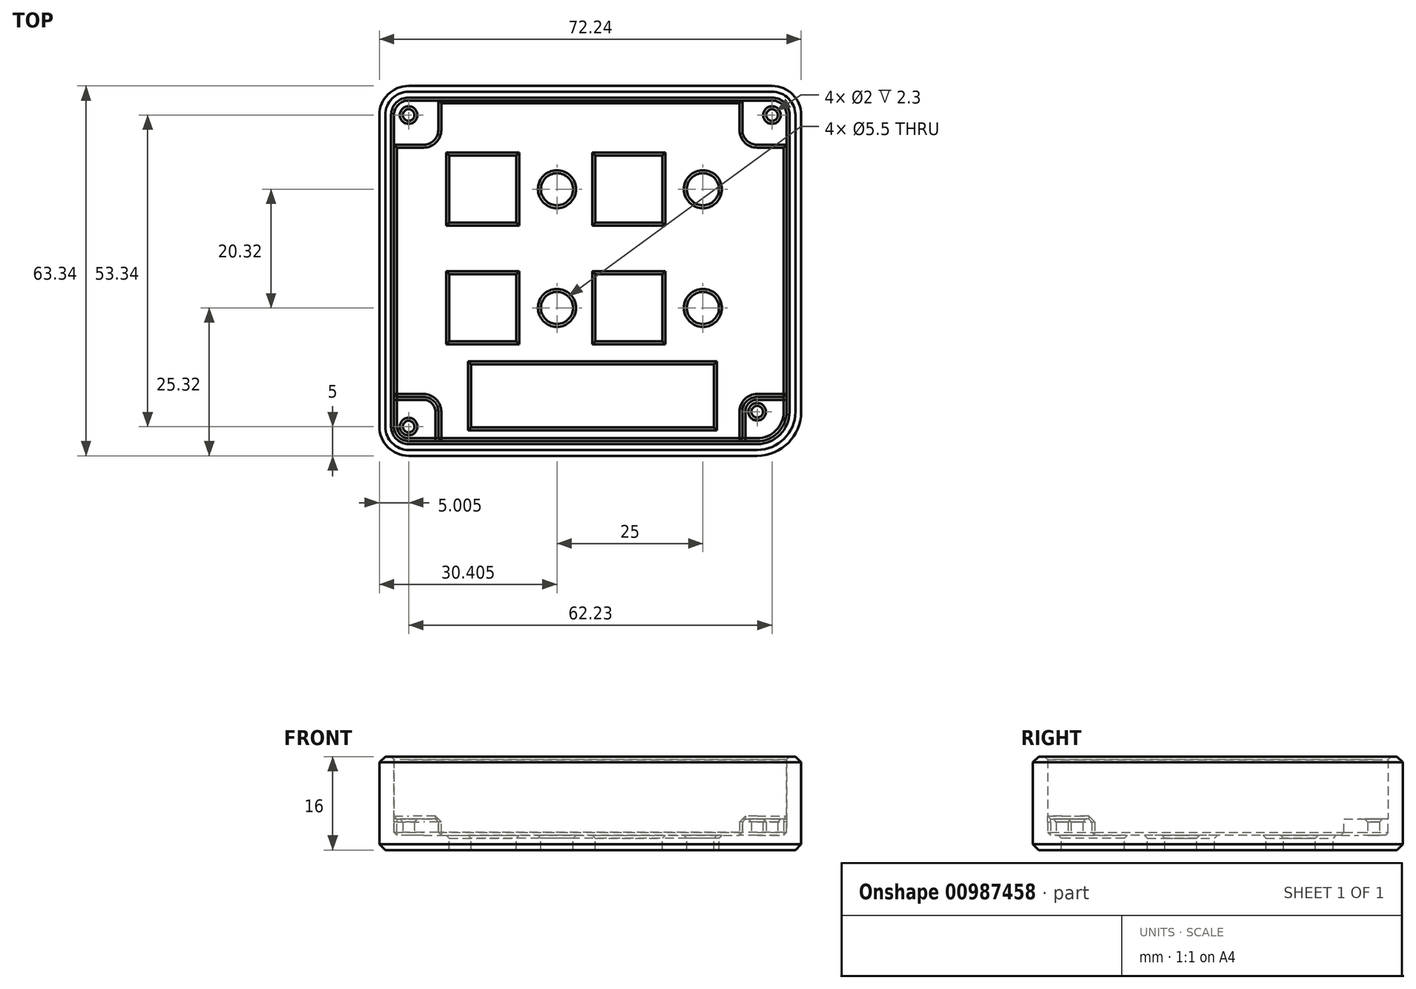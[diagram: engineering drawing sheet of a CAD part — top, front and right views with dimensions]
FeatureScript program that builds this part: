
annotation { "Feature Type Name" : "Feature", "Feature Type Description" : "" }
export const myFeature = defineFeature(function(context is Context, id is Id, definition is map)
    precondition{}
    {
        {
            var Q0;
            Q0=qCreatedBy(makeId("Top.planeOp"),FACE);
            var sketch = newSketch(context, id + "F0", { "sketchPlane" : qUnion([Q0])});
            skLineSegment(sketch, "E0.bottom", {"start": v(28.58, -31.67) * mm, "end": v(-31.11, -31.67) * mm});
            skLineSegment(sketch, "E0.top", {"start": v(31.11, 31.67) * mm, "end": v(-31.12, 31.67) * mm});
            skLineSegment(sketch, "E0.left", {"start": v(36.12, -24.13) * mm, "end": v(36.12, 26.67) * mm});
            skLineSegment(sketch, "E0.right", {"start": v(-36.11, -26.67) * mm, "end": v(-36.12, 26.67) * mm});
            skPoint(sketch, "E0.middle", {"position": v(0, 0) * mm});
            skCircle(sketch, "E1", {"center": v(-31.11, 26.67) * mm, "radius": 1 * mm});
            skCircle(sketch, "E2", {"center": v(-31.11, -26.67) * mm, "radius": 1 * mm});
            skCircle(sketch, "E3", {"center": v(31.11, 26.67) * mm, "radius": 1 * mm});
            skCircle(sketch, "E4", {"center": v(28.58, -24.13) * mm, "radius": 1 * mm});
            skPoint(sketch, "E5.visualSharp", {"position": v(-36.12, 31.67) * mm});
            skArc(sketch, "E5.filletArc", {"start": v(-31.12, 31.67) * mm, "mid": v(-34.65, 30.2) * mm, "end": v(-36.12, 26.67) * mm});
            skPoint(sketch, "E6.visualSharp", {"position": v(36.11, 31.67) * mm});
            skArc(sketch, "E6.filletArc", {"start": v(36.12, 26.67) * mm, "mid": v(34.65, 30.2) * mm, "end": v(31.11, 31.67) * mm});
            skPoint(sketch, "E7.visualSharp", {"position": v(36.12, -31.67) * mm});
            skArc(sketch, "E7.filletArc", {"start": v(28.58, -31.67) * mm, "mid": v(33.9, -29.46) * mm, "end": v(36.12, -24.13) * mm});
            skPoint(sketch, "E8.visualSharp", {"position": v(-36.11, -31.67) * mm});
            skArc(sketch, "E8.filletArc", {"start": v(-36.11, -26.67) * mm, "mid": v(-34.65, -30.2) * mm, "end": v(-31.11, -31.67) * mm});
            skLineSegment(sketch, "E9", {"start": v(-26.04, 31.67) * mm, "end": v(-26.04, 24.13) * mm});
            skLineSegment(sketch, "E10", {"start": v(-28.58, 21.59) * mm, "end": v(-36.11, 21.59) * mm});
            skPoint(sketch, "E11.visualSharp", {"position": v(-26.04, 21.59) * mm});
            skArc(sketch, "E11.filletArc", {"start": v(-28.58, 21.59) * mm, "mid": v(-26.78, 22.33) * mm, "end": v(-26.04, 24.13) * mm});
            skLineSegment(sketch, "E12.MirrorCS", {"start": v(28.58, 21.59) * mm, "end": v(36.11, 21.59) * mm});
            skArc(sketch, "E13.MirrorCS", {"start": v(28.58, 21.59) * mm, "mid": v(26.78, 22.33) * mm, "end": v(26.04, 24.13) * mm});
            skLineSegment(sketch, "E14.MirrorCS", {"start": v(26.04, 31.67) * mm, "end": v(26.04, 24.13) * mm});
            skLineSegment(sketch, "E15.MirrorCS", {"start": v(-26.04, -31.67) * mm, "end": v(-26.04, -24.13) * mm});
            skArc(sketch, "E16.MirrorCS", {"start": v(-28.58, -21.59) * mm, "mid": v(-26.78, -22.33) * mm, "end": v(-26.04, -24.13) * mm});
            skLineSegment(sketch, "E17.MirrorCS", {"start": v(-28.58, -21.59) * mm, "end": v(-36.11, -21.59) * mm});
            skLineSegment(sketch, "E18.MirrorCS", {"start": v(28.58, -21.59) * mm, "end": v(36.11, -21.59) * mm});
            skArc(sketch, "E19.MirrorCS", {"start": v(28.58, -21.59) * mm, "mid": v(26.78, -22.33) * mm, "end": v(26.04, -24.13) * mm});
            skLineSegment(sketch, "E20.MirrorCS", {"start": v(26.04, -31.67) * mm, "end": v(26.04, -24.13) * mm});
            skSolve(sketch);
        }
        {
            var Q0;
            Q0=makeQuery(id+"F0.imprint","IMPRINT",FACE,{"disambiguationData":[TD([[makeQuery(id+"F0.imprint","IMPRINT",EDGE,{"derivedFrom":sQuery(id+"F0.wireOp",EDGE,"E0.bottom")}),-1.0]])]});
            var Q1;
            Q1=makeQuery(id+"F0.imprint","IMPRINT",FACE,{"disambiguationData":[TD([[makeQuery(id+"F0.imprint","IMPRINT",EDGE,{"derivedFrom":sQuery(id+"F0.wireOp",EDGE,"E1")}),-1.0]])]});
            var Q2;
            {var subQ4=sQuery(id+"F0.wireOp",EDGE,"E9");Q2=makeQuery(id+"F0.imprint","IMPRINT",FACE,{"disambiguationData":[TD([[makeQuery(id+"F0.imprint","IMPRINT",EDGE,{"derivedFrom":subQ4}),1.0]])]});}
            var Q3;
            Q3=makeQuery(id+"F0.imprint","IMPRINT",FACE,{"disambiguationData":[TD([[makeQuery(id+"F0.imprint","IMPRINT",EDGE,{"derivedFrom":sQuery(id+"F0.wireOp",EDGE,"E3")}),-1.0]])]});
            var Q4;
            Q4=makeQuery(id+"F0.imprint","IMPRINT",FACE,{"disambiguationData":[TD([[makeQuery(id+"F0.imprint","IMPRINT",EDGE,{"derivedFrom":sQuery(id+"F0.wireOp",EDGE,"E3")}),1.0]])]});
            var Q5;
            Q5=makeQuery(id+"F0.imprint","IMPRINT",FACE,{"disambiguationData":[TD([[makeQuery(id+"F0.imprint","IMPRINT",EDGE,{"derivedFrom":sQuery(id+"F0.wireOp",EDGE,"E1")}),1.0]])]});
            var Q6;
            Q6=makeQuery(id+"F0.imprint","IMPRINT",FACE,{"disambiguationData":[TD([[makeQuery(id+"F0.imprint","IMPRINT",EDGE,{"derivedFrom":sQuery(id+"F0.wireOp",EDGE,"E2")}),1.0]])]});
            var Q7;
            Q7=makeQuery(id+"F0.imprint","IMPRINT",FACE,{"disambiguationData":[TD([[makeQuery(id+"F0.imprint","IMPRINT",EDGE,{"derivedFrom":sQuery(id+"F0.wireOp",EDGE,"E4")}),1.0]])]});
            extrude(context, id + "F1", {"entities" : qUnion([Q0, Q1, Q2, Q3, Q4, Q5, Q6, Q7]), "depth" : 16 * mm, "offsetDistance" : 25 * mm});
        }
        {
            var Q0;
            Q0=makeQuery(id+"F1.opExtrude","CAP_FACE",FACE,{"disambiguationData":[OSD([sQuery(id+"F0.wireOp",EDGE,"E0.bottom"),sQuery(id+"F0.wireOp",EDGE,"E0.top"),sQuery(id+"F0.wireOp",EDGE,"E0.left"),sQuery(id+"F0.wireOp",EDGE,"E0.right"),sQuery(id+"F0.wireOp",EDGE,"E5.filletArc"),sQuery(id+"F0.wireOp",EDGE,"E6.filletArc"),sQuery(id+"F0.wireOp",EDGE,"E7.filletArc"),sQuery(id+"F0.wireOp",EDGE,"E8.filletArc")])],"isStart":false});
            shell(context, id + "F2", {"entities" : qUnion([Q0]), "thickness" : 2.5 * mm});
        }
        {
            var Q0;
            Q0=makeQuery(id+"F0.imprint","IMPRINT",FACE,{"disambiguationData":[TD([[makeQuery(id+"F0.imprint","IMPRINT",EDGE,{"derivedFrom":sQuery(id+"F0.wireOp",EDGE,"E2")}),-1.0]])]});
            var Q1;
            Q1=makeQuery(id+"F0.imprint","IMPRINT",FACE,{"disambiguationData":[TD([[makeQuery(id+"F0.imprint","IMPRINT",EDGE,{"derivedFrom":sQuery(id+"F0.wireOp",EDGE,"E4")}),-1.0]])]});
            var Q2;
            Q2=makeQuery(id+"F0.imprint","IMPRINT",FACE,{"disambiguationData":[TD([[makeQuery(id+"F0.imprint","IMPRINT",EDGE,{"derivedFrom":sQuery(id+"F0.wireOp",EDGE,"E3")}),-1.0]])]});
            var Q3;
            Q3=makeQuery(id+"F0.imprint","IMPRINT",FACE,{"disambiguationData":[TD([[makeQuery(id+"F0.imprint","IMPRINT",EDGE,{"derivedFrom":sQuery(id+"F0.wireOp",EDGE,"E1")}),-1.0]])]});
            extrude(context, id + "F3", {"entities" : qUnion([Q0, Q1, Q2, Q3]), "operationType" : NewBodyOperationType.ADD, "depth" : 5.3 * mm, "offsetDistance" : 25 * mm});
        }
        {
            var Q0;
            {var subQ0=sQuery(id+"F0.wireOp",EDGE,"E0.bottom");var subQ1=sQuery(id+"F0.wireOp",EDGE,"E0.top");var subQ2=sQuery(id+"F0.wireOp",EDGE,"E0.left");var subQ3=sQuery(id+"F0.wireOp",EDGE,"E0.right");Q0=makeQuery(id+"F3.boolean.opBoolean","SPLIT",FACE,{"disambiguationData":[TD([makeQuery(id+"F2.opShell","OFFSET_FACE",FACE,{"disambiguationData":[OSD([subQ0])]})])],"derivedFrom":makeQuery(id+"F2.opShell","OFFSET_FACE",FACE,{"disambiguationData":[OSD([subQ0,subQ1,subQ2,subQ3,sQuery(id+"F0.wireOp",EDGE,"E5.filletArc"),sQuery(id+"F0.wireOp",EDGE,"E6.filletArc"),sQuery(id+"F0.wireOp",EDGE,"E7.filletArc"),sQuery(id+"F0.wireOp",EDGE,"E8.filletArc")])]})});}
            var sketch = newSketch(context, id + "F4", { "sketchPlane" : qUnion([Q0])});
            skLineSegment(sketch, "E21.bottom", {"start": v(-20.45, -16.02) * mm, "end": v(21.18, -16.02) * mm});
            skLineSegment(sketch, "E21.top", {"start": v(-20.45, -26.82) * mm, "end": v(21.19, -26.82) * mm});
            skLineSegment(sketch, "E21.left", {"start": v(-20.45, -16.02) * mm, "end": v(-20.45, -26.82) * mm});
            skLineSegment(sketch, "E21.right", {"start": v(21.19, -16.02) * mm, "end": v(21.19, -26.82) * mm});
            skLineSegment(sketch, "E22.bottom", {"start": v(-12.67, 8.22) * mm, "end": v(-24.17, 8.22) * mm});
            skLineSegment(sketch, "E22.top", {"start": v(-12.66, 19.72) * mm, "end": v(-24.16, 19.72) * mm});
            skLineSegment(sketch, "E22.left", {"start": v(-12.67, 8.22) * mm, "end": v(-12.66, 19.72) * mm});
            skLineSegment(sketch, "E22.right", {"start": v(-24.17, 8.22) * mm, "end": v(-24.16, 19.72) * mm});
            skPoint(sketch, "E22.middle", {"position": v(-18.41, 13.97) * mm});
            skCircle(sketch, "E23", {"center": v(-5.72, 13.97) * mm, "radius": 2.75 * mm});
            skLineSegment(sketch, "E24.0.1.0", {"start": v(-12.67, -12.1) * mm, "end": v(-12.66, -0.6) * mm});
            skCircle(sketch, "E24.0.1.1", {"center": v(-5.72, -6.35) * mm, "radius": 2.75 * mm});
            skLineSegment(sketch, "E24.0.1.2", {"start": v(-24.17, -12.1) * mm, "end": v(-24.16, -0.6) * mm});
            skPoint(sketch, "E24.0.1.3", {"position": v(-18.41, -6.35) * mm});
            skLineSegment(sketch, "E24.0.1.4", {"start": v(-12.67, -12.1) * mm, "end": v(-24.17, -12.1) * mm});
            skLineSegment(sketch, "E24.0.1.5", {"start": v(-12.66, -0.6) * mm, "end": v(-24.16, -0.6) * mm});
            skLineSegment(sketch, "E24.1.0.0", {"start": v(12.33, 8.22) * mm, "end": v(12.34, 19.72) * mm});
            skCircle(sketch, "E24.1.0.1", {"center": v(19.29, 13.97) * mm, "radius": 2.75 * mm});
            skLineSegment(sketch, "E24.1.0.2", {"start": v(0.84, 8.22) * mm, "end": v(0.84, 19.72) * mm});
            skPoint(sketch, "E24.1.0.3", {"position": v(6.59, 13.97) * mm});
            skLineSegment(sketch, "E24.1.0.4", {"start": v(12.33, 8.22) * mm, "end": v(0.83, 8.22) * mm});
            skLineSegment(sketch, "E24.1.0.5", {"start": v(12.34, 19.72) * mm, "end": v(0.84, 19.72) * mm});
            skLineSegment(sketch, "E24.1.1.0", {"start": v(12.33, -12.1) * mm, "end": v(12.34, -0.6) * mm});
            skCircle(sketch, "E24.1.1.1", {"center": v(19.29, -6.35) * mm, "radius": 2.75 * mm});
            skLineSegment(sketch, "E24.1.1.2", {"start": v(0.84, -12.1) * mm, "end": v(0.84, -0.6) * mm});
            skPoint(sketch, "E24.1.1.3", {"position": v(6.59, -6.35) * mm});
            skLineSegment(sketch, "E24.1.1.4", {"start": v(12.33, -12.1) * mm, "end": v(0.83, -12.1) * mm});
            skLineSegment(sketch, "E24.1.1.5", {"start": v(12.34, -0.6) * mm, "end": v(0.84, -0.6) * mm});
            skLineSegment(sketch, "E24.direction1", {"start": v(-24.17, 8.22) * mm, "end": v(0.83, 8.22) * mm, "construction": true});
            skLineSegment(sketch, "E24.direction2", {"start": v(-24.17, 8.22) * mm, "end": v(-24.17, -12.1) * mm, "construction": true});
            skSolve(sketch);
        }
        {
            var Q0;
            Q0=makeQuery(id+"F4.imprint","IMPRINT",FACE,{"disambiguationData":[TD([[makeQuery(id+"F4.imprint","IMPRINT",EDGE,{"derivedFrom":sQuery(id+"F4.wireOp",EDGE,"E22.bottom")}),-1.0]])]});
            var Q1;
            Q1=makeQuery(id+"F4.imprint","IMPRINT",FACE,{"disambiguationData":[TD([[makeQuery(id+"F4.imprint","IMPRINT",EDGE,{"derivedFrom":sQuery(id+"F4.wireOp",EDGE,"E24.0.1.0")}),1.0]])]});
            var Q2;
            Q2=makeQuery(id+"F4.imprint","IMPRINT",FACE,{"disambiguationData":[TD([[makeQuery(id+"F4.imprint","IMPRINT",EDGE,{"derivedFrom":sQuery(id+"F4.wireOp",EDGE,"E23")}),1.0]])]});
            var Q3;
            Q3=makeQuery(id+"F4.imprint","IMPRINT",FACE,{"disambiguationData":[TD([[makeQuery(id+"F4.imprint","IMPRINT",EDGE,{"derivedFrom":sQuery(id+"F4.wireOp",EDGE,"E24.0.1.1")}),1.0]])]});
            var Q4;
            Q4=makeQuery(id+"F4.imprint","IMPRINT",FACE,{"disambiguationData":[TD([[makeQuery(id+"F4.imprint","IMPRINT",EDGE,{"derivedFrom":sQuery(id+"F4.wireOp",EDGE,"E24.1.1.0")}),1.0]])]});
            var Q5;
            Q5=makeQuery(id+"F4.imprint","IMPRINT",FACE,{"disambiguationData":[TD([[makeQuery(id+"F4.imprint","IMPRINT",EDGE,{"derivedFrom":sQuery(id+"F4.wireOp",EDGE,"E24.1.0.0")}),1.0]])]});
            var Q6;
            Q6=makeQuery(id+"F4.imprint","IMPRINT",FACE,{"disambiguationData":[TD([[makeQuery(id+"F4.imprint","IMPRINT",EDGE,{"derivedFrom":sQuery(id+"F4.wireOp",EDGE,"E24.1.0.1")}),1.0]])]});
            var Q7;
            Q7=makeQuery(id+"F4.imprint","IMPRINT",FACE,{"disambiguationData":[TD([[makeQuery(id+"F4.imprint","IMPRINT",EDGE,{"derivedFrom":sQuery(id+"F4.wireOp",EDGE,"E24.1.1.1")}),1.0]])]});
            var Q8;
            Q8=makeQuery(id+"F4.imprint","IMPRINT",FACE,{"disambiguationData":[TD([[makeQuery(id+"F4.imprint","IMPRINT",EDGE,{"derivedFrom":sQuery(id+"F4.wireOp",EDGE,"E21.bottom")}),-1.0]])]});
            extrude(context, id + "F5", {"entities" : qUnion([Q0, Q1, Q2, Q3, Q4, Q5, Q6, Q7, Q8]), "operationType" : NewBodyOperationType.REMOVE, "endBound" : BoundingType.THROUGH_ALL, "oppositeDirection" : true, "depth" : 25 * mm, "offsetDistance" : 25 * mm});
        }
        {
            var Q0;
            Q0=makeQuery(id+"F1.opExtrude","CAP_EDGE",EDGE,{"disambiguationData":[OSD([sQuery(id+"F0.wireOp",EDGE,"E0.right")])],"isStart":false});
            var Q1;
            Q1=makeQuery(id+"F1.opExtrude","CAP_EDGE",EDGE,{"disambiguationData":[OSD([sQuery(id+"F0.wireOp",EDGE,"E5.filletArc")])],"isStart":false});
            var Q2;
            Q2=makeQuery(id+"F1.opExtrude","CAP_EDGE",EDGE,{"disambiguationData":[OSD([sQuery(id+"F0.wireOp",EDGE,"E0.top")])],"isStart":false});
            var Q3;
            Q3=makeQuery(id+"F1.opExtrude","CAP_EDGE",EDGE,{"disambiguationData":[OSD([sQuery(id+"F0.wireOp",EDGE,"E6.filletArc")])],"isStart":false});
            var Q4;
            Q4=makeQuery(id+"F1.opExtrude","CAP_EDGE",EDGE,{"disambiguationData":[OSD([sQuery(id+"F0.wireOp",EDGE,"E0.left")])],"isStart":false});
            var Q5;
            Q5=makeQuery(id+"F1.opExtrude","CAP_EDGE",EDGE,{"disambiguationData":[OSD([sQuery(id+"F0.wireOp",EDGE,"E7.filletArc")])],"isStart":false});
            var Q6;
            Q6=makeQuery(id+"F1.opExtrude","CAP_EDGE",EDGE,{"disambiguationData":[OSD([sQuery(id+"F0.wireOp",EDGE,"E0.bottom")])],"isStart":false});
            var Q7;
            Q7=makeQuery(id+"F1.opExtrude","CAP_EDGE",EDGE,{"disambiguationData":[OSD([sQuery(id+"F0.wireOp",EDGE,"E8.filletArc")])],"isStart":true});
            var Q8;
            Q8=makeQuery(id+"F1.opExtrude","CAP_EDGE",EDGE,{"disambiguationData":[OSD([sQuery(id+"F0.wireOp",EDGE,"E8.filletArc")])],"isStart":false});
            chamfer(context, id + "F6", {"entities" : qUnion([Q0, Q1, Q2, Q3, Q4, Q5, Q6, Q7, Q8]), "width" : 1 * mm, "tangentPropagation" : true});
        }
        {
            var Q0;
            Q0=makeQuery(id+"F3.opExtrude","CAP_FACE",FACE,{"disambiguationData":[OSD([sQuery(id+"F0.wireOp",EDGE,"E0.bottom"),sQuery(id+"F0.wireOp",EDGE,"E0.right"),sQuery(id+"F0.wireOp",EDGE,"E2"),sQuery(id+"F0.wireOp",EDGE,"E8.filletArc"),sQuery(id+"F0.wireOp",EDGE,"E15.MirrorCS"),sQuery(id+"F0.wireOp",EDGE,"E16.MirrorCS"),sQuery(id+"F0.wireOp",EDGE,"E17.MirrorCS")])],"isStart":false});
            var Q1;
            {var subQ0=sQuery(id+"F0.wireOp",EDGE,"E0.bottom");var subQ1=sQuery(id+"F0.wireOp",EDGE,"E0.top");var subQ2=sQuery(id+"F0.wireOp",EDGE,"E0.left");var subQ3=sQuery(id+"F0.wireOp",EDGE,"E0.right");Q1=makeQuery(id+"F3.boolean.opBoolean","SPLIT",FACE,{"disambiguationData":[TD([makeQuery(id+"F2.opShell","OFFSET_FACE",FACE,{"disambiguationData":[OSD([subQ0])]})])],"derivedFrom":makeQuery(id+"F2.opShell","OFFSET_FACE",FACE,{"disambiguationData":[OSD([subQ0,subQ1,subQ2,subQ3,sQuery(id+"F0.wireOp",EDGE,"E5.filletArc"),sQuery(id+"F0.wireOp",EDGE,"E6.filletArc"),sQuery(id+"F0.wireOp",EDGE,"E7.filletArc"),sQuery(id+"F0.wireOp",EDGE,"E8.filletArc")])]})});}
            var Q2;
            {var subQ0=sQuery(id+"F0.wireOp",EDGE,"E0.right");Q2=makeQuery(id+"F2.opShell","OFFSET_EDGE",EDGE,{"disambiguationData":[OSD([subQ0]),TDD([makeQuery(id+"F1.opExtrude","CAP_EDGE",EDGE,{"disambiguationData":[OSD([subQ0])],"isStart":false})])]});}
            var Q3;
            Q3=makeQuery(id+"F3.opExtrude","CAP_EDGE",EDGE,{"disambiguationData":[OSD([sQuery(id+"F0.wireOp",EDGE,"E1")])],"isStart":false});
            var Q4;
            {var subQ0=sQuery(id+"F0.wireOp",EDGE,"E0.top");Q4=makeQuery(id+"F2.opShell","OFFSET_EDGE",EDGE,{"disambiguationData":[OSD([subQ0]),TDD([makeQuery(id+"F1.opExtrude","CAP_EDGE",EDGE,{"disambiguationData":[OSD([subQ0])],"isStart":false})])]});}
            var Q5;
            {var subQ0=sQuery(id+"F0.wireOp",EDGE,"E5.filletArc");Q5=makeQuery(id+"F2.opShell","OFFSET_EDGE",EDGE,{"disambiguationData":[OSD([subQ0]),TDD([makeQuery(id+"F1.opExtrude","CAP_EDGE",EDGE,{"disambiguationData":[OSD([subQ0])],"isStart":false})])]});}
            var Q6;
            {var subQ0=sQuery(id+"F0.wireOp",EDGE,"E6.filletArc");Q6=makeQuery(id+"F2.opShell","OFFSET_EDGE",EDGE,{"disambiguationData":[OSD([subQ0]),TDD([makeQuery(id+"F1.opExtrude","CAP_EDGE",EDGE,{"disambiguationData":[OSD([subQ0])],"isStart":false})])]});}
            var Q7;
            Q7=makeQuery(id+"F3.opExtrude","CAP_EDGE",EDGE,{"disambiguationData":[OSD([sQuery(id+"F0.wireOp",EDGE,"E3")])],"isStart":false});
            var Q8;
            Q8=makeQuery(id+"F3.opExtrude","CAP_FACE",FACE,{"disambiguationData":[OSD([sQuery(id+"F0.wireOp",EDGE,"E0.bottom"),sQuery(id+"F0.wireOp",EDGE,"E0.left"),sQuery(id+"F0.wireOp",EDGE,"E4"),sQuery(id+"F0.wireOp",EDGE,"E7.filletArc"),sQuery(id+"F0.wireOp",EDGE,"E18.MirrorCS"),sQuery(id+"F0.wireOp",EDGE,"E19.MirrorCS"),sQuery(id+"F0.wireOp",EDGE,"E20.MirrorCS")])],"isStart":false});
            var Q9;
            Q9=makeQuery(id+"F3.opExtrude","CAP_EDGE",EDGE,{"disambiguationData":[OSD([sQuery(id+"F0.wireOp",EDGE,"E4")])],"isStart":false});
            chamfer(context, id + "F7", {"entities" : qUnion([Q0, Q1, Q2, Q3, Q4, Q5, Q6, Q7, Q8, Q9]), "width" : .5 * mm, "tangentPropagation" : true});
        }
    });
